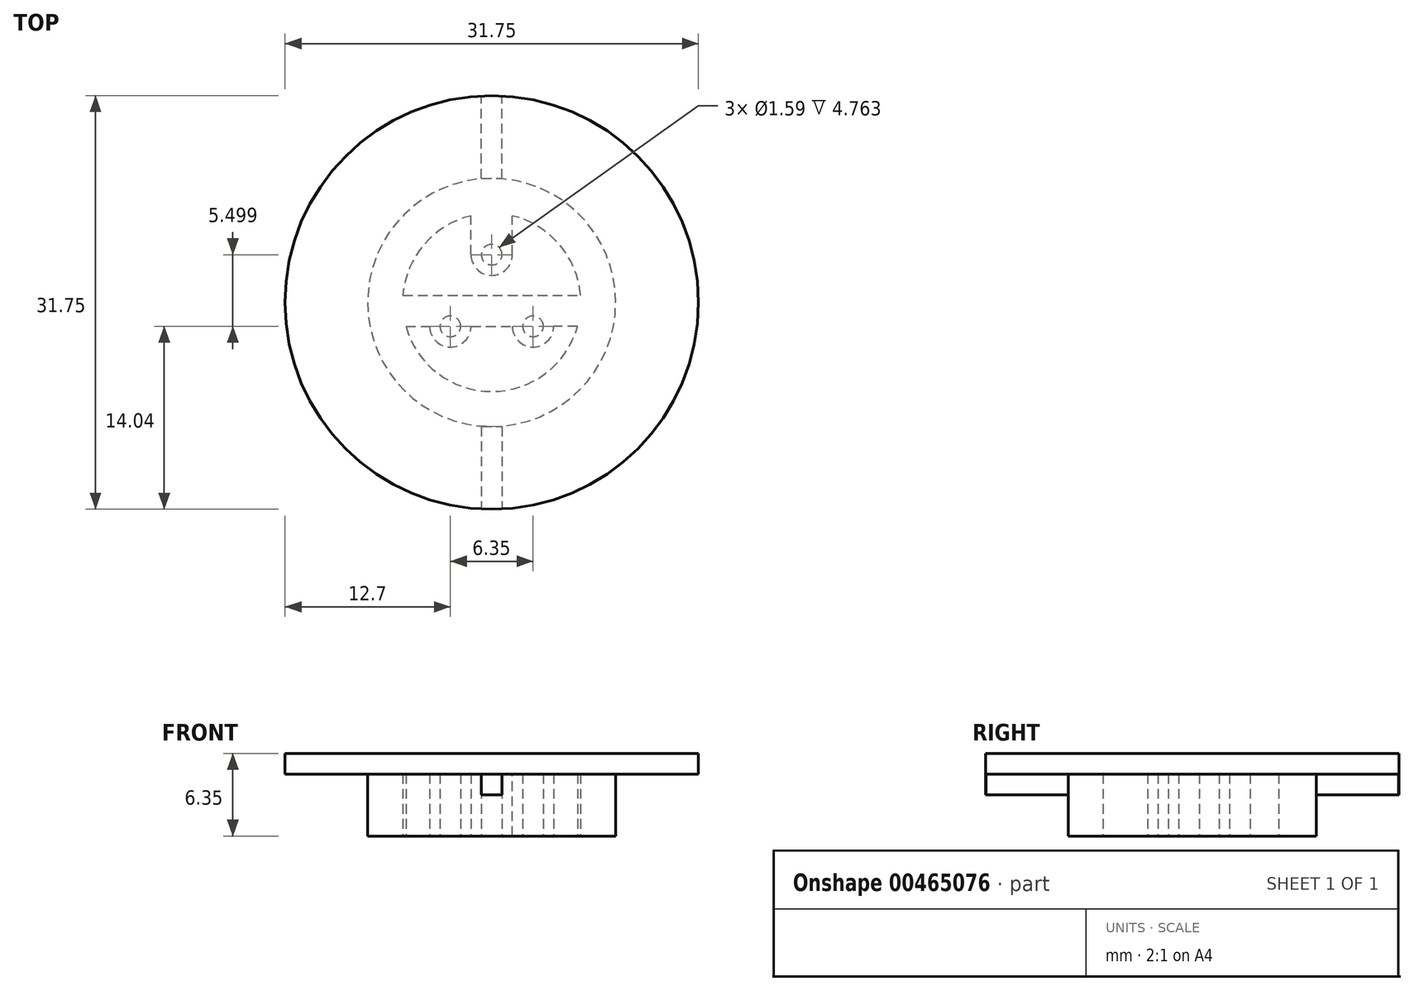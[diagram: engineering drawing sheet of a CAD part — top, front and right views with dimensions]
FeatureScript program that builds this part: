
annotation { "Feature Type Name" : "Feature", "Feature Type Description" : "" }
export const myFeature = defineFeature(function(context is Context, id is Id, definition is map)
    precondition{}
    {
        {
            var Q0;
            Q0=qCreatedBy(makeId("Top.planeOp"),FACE);
            var sketch = newSketch(context, id + "F0", { "sketchPlane" : qUnion([Q0])});
            skLineSegment(sketch, "E0", {"start": v(0, 0) * mm, "end": v(6.35, 0) * mm, "construction": true});
            skLineSegment(sketch, "E1", {"start": v(6.35, 0) * mm, "end": v(3.18, 5.5) * mm, "construction": true});
            skLineSegment(sketch, "E2", {"start": v(3.18, 5.5) * mm, "end": v(0, 0) * mm, "construction": true});
            skCircle(sketch, "E3", {"center": v(3.18, 5.5) * mm, "radius": 0.8 * mm});
            skCircle(sketch, "E4", {"center": v(6.35, 0) * mm, "radius": 0.8 * mm});
            skCircle(sketch, "E5", {"center": v(0, 0) * mm, "radius": 0.8 * mm});
            skCircle(sketch, "E6", {"center": v(3.18, 5.5) * mm, "radius": 1.59 * mm});
            skCircle(sketch, "E7", {"center": v(6.35, 0) * mm, "radius": 1.59 * mm});
            skCircle(sketch, "E8", {"center": v(0, 0) * mm, "radius": 1.59 * mm});
            skCircle(sketch, "E9", {"center": v(3.18, 1.83) * mm, "radius": 5.25 * mm, "construction": true});
            skCircle(sketch, "E10", {"center": v(3.18, 1.83) * mm, "radius": 6.84 * mm});
            skCircle(sketch, "E11", {"center": v(3.18, 1.83) * mm, "radius": 9.53 * mm});
            skSolve(sketch);
        }
        {
            var Q0;
            Q0=makeQuery(id+"F0.imprint","IMPRINT",FACE,{"disambiguationData":[TD([[makeQuery(id+"F0.imprint","IMPRINT",EDGE,{"derivedFrom":sQuery(id+"F0.wireOp",EDGE,"E3")}),-1.0]])]});
            var Q1;
            Q1=makeQuery(id+"F0.imprint","IMPRINT",FACE,{"disambiguationData":[TD([[makeQuery(id+"F0.imprint","IMPRINT",EDGE,{"derivedFrom":sQuery(id+"F0.wireOp",EDGE,"E5")}),-1.0]])]});
            var Q2;
            Q2=makeQuery(id+"F0.imprint","IMPRINT",FACE,{"disambiguationData":[TD([[makeQuery(id+"F0.imprint","IMPRINT",EDGE,{"derivedFrom":sQuery(id+"F0.wireOp",EDGE,"E4")}),-1.0]])]});
            var Q3;
            Q3=makeQuery(id+"F0.imprint","IMPRINT",FACE,{"disambiguationData":[TD([[makeQuery(id+"F0.imprint","IMPRINT",EDGE,{"derivedFrom":sQuery(id+"F0.wireOp",EDGE,"E10")}),-1.0]])]});
            extrude(context, id + "F1", {"entities" : qUnion([Q0, Q1, Q2, Q3]), "depth" : 4.76 * mm});
        }
        {
            var Q0;
            Q0=makeQuery(id+"F1.opExtrude","CAP_FACE",FACE,{"disambiguationData":[OSD([sQuery(id+"F0.wireOp",EDGE,"E10"),sQuery(id+"F0.wireOp",EDGE,"E11")])],"isStart":false});
            var sketch = newSketch(context, id + "F2", { "sketchPlane" : qUnion([Q0])});
            skCircle(sketch, "E12", {"center": v(3.18, 1.83) * mm, "radius": 15.88 * mm});
            skSolve(sketch);
        }
        {
            var Q0;
            Q0 = qSketchRegion(id + "F2", true);
            extrude(context, id + "F3", {"entities" : qUnion([Q0]), "operationType" : NewBodyOperationType.ADD, "depth" : 1.59 * mm});
        }
        {
            var Q0;
            Q0=makeQuery(id+"F3.opExtrude","CAP_FACE",FACE,{"disambiguationData":[OSD([sQuery(id+"F2.wireOp",EDGE,"E12")])],"isStart":true});
            var sketch = newSketch(context, id + "F4", { "sketchPlane" : qUnion([Q0])});
            skLineSegment(sketch, "E13.bottom", {"start": v(2.38, 7.7) * mm, "end": v(3.97, 7.7) * mm});
            skLineSegment(sketch, "E13.left", {"start": v(2.38, 7.7) * mm, "end": v(2.38, 14.02) * mm});
            skLineSegment(sketch, "E13.right", {"start": v(3.97, 7.7) * mm, "end": v(3.97, 14.02) * mm});
            skLineSegment(sketch, "E14.bottom", {"start": v(2.38, -11.36) * mm, "end": v(3.97, -11.36) * mm});
            skLineSegment(sketch, "E14.left", {"start": v(2.38, -11.36) * mm, "end": v(2.38, -17.69) * mm});
            skLineSegment(sketch, "E14.right", {"start": v(3.97, -11.36) * mm, "end": v(3.97, -17.69) * mm});
            skLineSegment(sketch, "E15", {"start": v(3.97, 7.7) * mm, "end": v(3.97, -11.36) * mm, "construction": true});
            skLineSegment(sketch, "E16", {"start": v(2.38, -11.36) * mm, "end": v(2.38, 7.7) * mm, "construction": true});
            skArc(sketch, "E17.0", {"start": v(3.97, 14.02) * mm, "mid": v(3.17, 14.04) * mm, "end": v(2.38, 14.02) * mm});
            skArc(sketch, "E18.trimOffspring", {"start": v(2.38, -17.69) * mm, "mid": v(3.17, -17.7) * mm, "end": v(3.97, -17.69) * mm});
            skSolve(sketch);
        }
        {
            var Q0;
            Q0 = qSketchRegion(id + "F4", true);
            extrude(context, id + "F5", {"entities" : qUnion([Q0]), "depth" : 1.59 * mm});
        }
        {
            var Q0;
            Q0=makeQuery(id+"F3.opExtrude","CAP_FACE",FACE,{"disambiguationData":[OSD([sQuery(id+"F2.wireOp",EDGE,"E12")])],"isStart":true});
            var sketch = newSketch(context, id + "F6", { "sketchPlane" : qUnion([Q0])});
            skLineSegment(sketch, "E19", {"start": v(0.8, 0) * mm, "end": v(5.56, 0) * mm});
            skLineSegment(sketch, "E20", {"start": v(10.01, 0) * mm, "end": v(7.14, 0) * mm});
            skLineSegment(sketch, "E21", {"start": v(-3.66, 0) * mm, "end": v(-0.8, 0) * mm});
            skArc(sketch, "E22.1", {"start": v(-0.8, 0) * mm, "mid": v(0, -0.8) * mm, "end": v(0.8, 0) * mm});
            skArc(sketch, "E22.2", {"start": v(5.56, 0) * mm, "mid": v(6.35, -0.8) * mm, "end": v(7.14, 0) * mm});
            skLineSegment(sketch, "E23", {"start": v(10.01, 0) * mm, "end": v(10.01, -1.59) * mm});
            skLineSegment(sketch, "E24", {"start": v(10.01, -1.59) * mm, "end": v(-3.66, -1.59) * mm});
            skLineSegment(sketch, "E25", {"start": v(-3.66, -1.59) * mm, "end": v(-3.66, 0) * mm});
            skArc(sketch, "E26.0", {"start": v(1.59, -5.5) * mm, "mid": v(3.18, -7.09) * mm, "end": v(4.76, -5.5) * mm});
            skLineSegment(sketch, "E27", {"start": v(4.76, -5.5) * mm, "end": v(4.76, -8.67) * mm});
            skLineSegment(sketch, "E28", {"start": v(1.59, -5.5) * mm, "end": v(1.59, -8.67) * mm});
            skLineSegment(sketch, "E29", {"start": v(1.59, -8.67) * mm, "end": v(4.76, -8.67) * mm});
            skSolve(sketch);
        }
        {
            var Q0;
            Q0 = qSketchRegion(id + "F6", true);
            var Q1;
            Q1=makeQuery(id+"F1.opExtrude","CAP_FACE",FACE,{"disambiguationData":[OSD([sQuery(id+"F0.wireOp",EDGE,"E4"),sQuery(id+"F0.wireOp",EDGE,"E7")])],"isStart":true});
            extrude(context, id + "F7", {"entities" : qUnion([Q0]), "operationType" : NewBodyOperationType.ADD, "endBound" : BoundingType.UP_TO_SURFACE, "endBoundEntityFace" : qUnion([Q1]), "depth" : 25.4 * mm});
        }
        {
            var Q0;
            {var subQ0=sQuery(id+"F0.wireOp",EDGE,"E7");var subQ1=sQuery(id+"F0.wireOp",EDGE,"E4");var subQ2=sQuery(id+"F6.wireOp",EDGE,"E19");var subQ3=sQuery(id+"F0.wireOp",EDGE,"E5");var subQ4=sQuery(id+"F0.wireOp",EDGE,"E8");Q0=makeQuery(id+"F7.boolean.opBoolean","MERGE",FACE,{"derivedFrom":[makeQuery(id+"F1.opExtrude","CAP_FACE",FACE,{"disambiguationData":[OSD([sQuery(id+"F0.wireOp",EDGE,"E3"),sQuery(id+"F0.wireOp",EDGE,"E6")])],"isStart":true}),makeQuery(id+"F1.opExtrude","CAP_FACE",FACE,{"disambiguationData":[OSD([subQ1,subQ0])],"isStart":true}),makeQuery(id+"F1.opExtrude","CAP_FACE",FACE,{"disambiguationData":[OSD([subQ3,subQ4])],"isStart":true}),makeQuery(id+"F1.opExtrude","CAP_FACE",FACE,{"disambiguationData":[OSD([sQuery(id+"F0.wireOp",EDGE,"E10"),sQuery(id+"F0.wireOp",EDGE,"E11")])],"isStart":true}),makeQuery(id+"F7.opExtrude","CAP_FACE",FACE,{"disambiguationData":[OSD([subQ1,subQ0]),ownerDisambiguation([makeQuery(id+"F6.imprint","IMPRINT",EDGE,{"disambiguationData":[TD([[makeQuery(id+"F6.imprint","INTERSECT",VERTEX,{"derivedFrom":[makeQuery(id+"F1.opExtrude","CAP_EDGE",EDGE,{"disambiguationData":[OSD([subQ4])],"isStart":false}),subQ2]}),1.0]])],"derivedFrom":subQ2})])],"isStart":false}),makeQuery(id+"F7.opExtrude","CAP_FACE",FACE,{"disambiguationData":[OSD([subQ1,subQ0]),ownerDisambiguation([makeQuery(id+"F6.imprint","IMPRINT",EDGE,{"derivedFrom":sQuery(id+"F6.wireOp",EDGE,"E26.0")})])],"isStart":false})]});}
            var sketch = newSketch(context, id + "F8", { "sketchPlane" : qUnion([Q0])});
            skLineSegment(sketch, "E30.bottom", {"start": v(-3.67, -1.59) * mm, "end": v(10.02, -1.59) * mm});
            skLineSegment(sketch, "E30.top", {"start": v(-3.67, -2.38) * mm, "end": v(10.02, -2.38) * mm});
            skLineSegment(sketch, "E30.left", {"start": v(-3.67, -1.59) * mm, "end": v(-3.67, -2.38) * mm});
            skLineSegment(sketch, "E30.right", {"start": v(10.02, -1.59) * mm, "end": v(10.02, -2.38) * mm});
            skSolve(sketch);
        }
        {
            var Q0;
            Q0 = qSketchRegion(id + "F8", true);
            var Q1;
            {var subQ1=makeQuery(id+"F1.opExtrude","SWEPT_FACE",FACE,{"disambiguationData":[OSD([sQuery(id+"F0.wireOp",EDGE,"E6")])]});Q1=makeQuery(id+"F7.boolean.opBoolean","SPLIT",FACE,{"disambiguationData":[TD([subQ1])],"derivedFrom":makeQuery(id+"F3.boolean.opBoolean","SPLIT",FACE,{"disambiguationData":[TD([subQ1])],"derivedFrom":makeQuery(id+"F3.opExtrude","CAP_FACE",FACE,{"disambiguationData":[OSD([sQuery(id+"F2.wireOp",EDGE,"E12")])],"isStart":true})})});}
            extrude(context, id + "F9", {"entities" : qUnion([Q0]), "operationType" : NewBodyOperationType.ADD, "endBound" : BoundingType.UP_TO_SURFACE, "oppositeDirection" : true, "endBoundEntityFace" : qUnion([Q1]), "depth" : 25.4 * mm});
        }
    });
